# Revit family: Honeycomb_Shades-Lutron-Sivoia_QS_Triathlon
name_source: partatom
category: Specialty Equipment
revit_build: Autodesk Revit 2017 (Build: 20160225_1515(x64)
units: mm (PartAtom-declared; Revit-internal decimal feet)

## family parameters
Cut with Voids When Loaded = No
Host = Face
OmniClass Number = 23.30.60.14.21
OmniClass Title = Shades
Part Type = Normal
Room Calculation Point = No
Round Connector Dimension = Use Diameter
Shared = No

## types (5) — shared parameters
Assembly Code = E2010320
Default Elevation = 0' - 0"
Description = Manual Collapsing Honeycomb Shade
Finish = Metal - Lutron - White
Instruction Sheet Link = http://www.lutron.com
Light Gap = 0' - 0 3/4"
Manufacturer = Lutron Electronics Co., Inc
Manufacturer Fax Number = 610-282-1243
Model = Manual Shade
Mounting = Pocket Mount
Performance URL = http://www.lutron.com
Product Documentation Link = http://www.lutron.com
Product Name = Sivoia QS Triathlon Insulating Honeycomb Shades
Product Page URL = http://www.lutron.com
Series = Honeycomb Shades
Shade Material = Fabric - Lutron - Honeycomb Linen - White
URL = http://www.lutron.com
Version = 2017 - v1.0a
Video Link = https://www.youtube.com
Warranty URL = http://www.lutron.com
zero-valued in all types: Cost

## per-type parameters (varying)
| type | Include Cable Guide for Outside Mount |
| Inside Mount | No |
| Inside Mount Full Recess | No |
| Outside Mount On Trim | No |
| Outside Mount Above Trim | No |
| Outside Mount for Door | Yes |

## geometry (parser evidence)
native form markers: Extrusion x1, Sweep x5
no freeform markers — native parametric forms only
